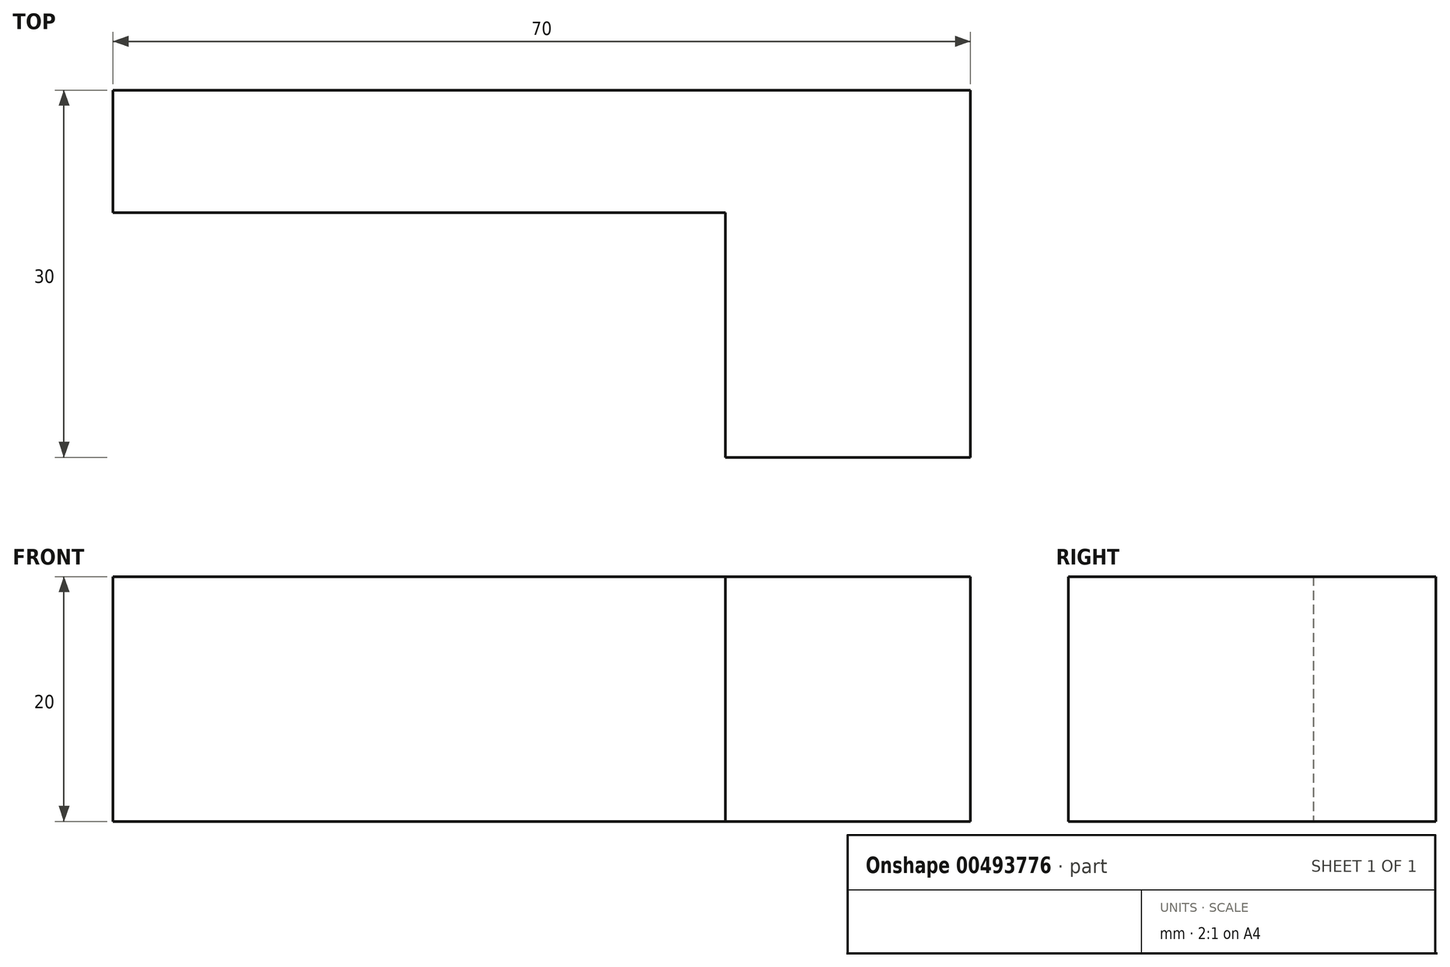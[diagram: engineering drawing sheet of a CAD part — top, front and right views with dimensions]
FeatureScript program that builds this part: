
annotation { "Feature Type Name" : "Feature", "Feature Type Description" : "" }
export const myFeature = defineFeature(function(context is Context, id is Id, definition is map)
    precondition{}
    {
        {
            var Q0;
            Q0=qCreatedBy(makeId("Top.planeOp"),FACE);
            var sketch = newSketch(context, id + "F0", { "sketchPlane" : qUnion([Q0])});
            skLineSegment(sketch, "E0", {"start": v(0, 30) * mm, "end": v(0, 20) * mm});
            skLineSegment(sketch, "E1", {"start": v(0, 20) * mm, "end": v(50, 20) * mm});
            skLineSegment(sketch, "E2", {"start": v(50, 20) * mm, "end": v(50, 0) * mm});
            skLineSegment(sketch, "E3", {"start": v(50, 0) * mm, "end": v(70, 0) * mm});
            skLineSegment(sketch, "E4", {"start": v(70, 0) * mm, "end": v(70, 30) * mm});
            skLineSegment(sketch, "E5", {"start": v(0, 30) * mm, "end": v(70, 30) * mm});
            skSolve(sketch);
        }
        {
            var Q0;
            Q0 = qSketchRegion(id + "F0", true);
            extrude(context, id + "F1", {"entities" : qUnion([Q0]), "depth" : 20 * mm});
        }
    });
